# Revit family: 3025586
name_source: partatom
category: Modelli generici
revit_build: Autodesk Revit 2018 (Build: 20170223_1515(x64)
units: mm (PartAtom-declared; Revit-internal decimal feet)

## family parameters
Basato su piano di lavoro = No
Condiviso = No
Punto di calcolo locali = No
Può ospitare armatura = No
Quota connettore circolare = Usa diametro
Sempre verticale = Sì
Taglio con vuoti quando caricato = No
Tipo di parte = Normale

## types (1)
- ARES CONDENSING 50 ErP
     GAS connection diameter = 25 mm  [stored 0.082021 ft]
    Boiler Material = Boiler Material
    Diameter of fume exhaust = 80 mm  [stored 0.262467 ft]
    Dimensions of Piping Connectors = 25 mm  [stored 0.082021 ft]
    Electric Power = 145 W
    Finishing Material = Boiler Material finishing
    Frequency of use = 50 Hz
    Hot water flow = 14.1 L/s
    Hydraulic Fittings = 2.5
    Manufacturer Product Link = https://www.immergas.com
    Mass = 90.00 kg
    MasterFormat = 23 00 00- Heating, Ventilating, and Air Conditioning (HVAC)
    Modello = ARES CONDENSING 50 ErP
    Name BIM&CO = Caldaia
    Nominal Current = 1 A
    Nominal Voltage = 230 V
    Operating Temperature = 90 °C
    Overall Depth = 645 mm  [stored 2.11614 ft]
    Overall Height = 1185 mm  [stored 3.8878 ft]
    Overall Width = 600 mm
    Piping volume boiler = 0 m³
    Product Code = 3.025586
    Produttore = Immergas
    Thermal flow rate = 50800
    Thermal power 80/60°C = 50000 W
    Uniformat = Heat Generating Systems
    Uniformat code = D3020
    yield hvac heating load nominal (%) = 98.5
    yield hvac heating load nominal 30 (%) = 96

note: source unit labels omitted for Thermal flow rate — the stored unit's dimension contradicts the parameter name (converter mislabeling)

note: [stored X ft] marks values corroborated as IEEE doubles in the binary element streams (Revit-internal decimal feet)
